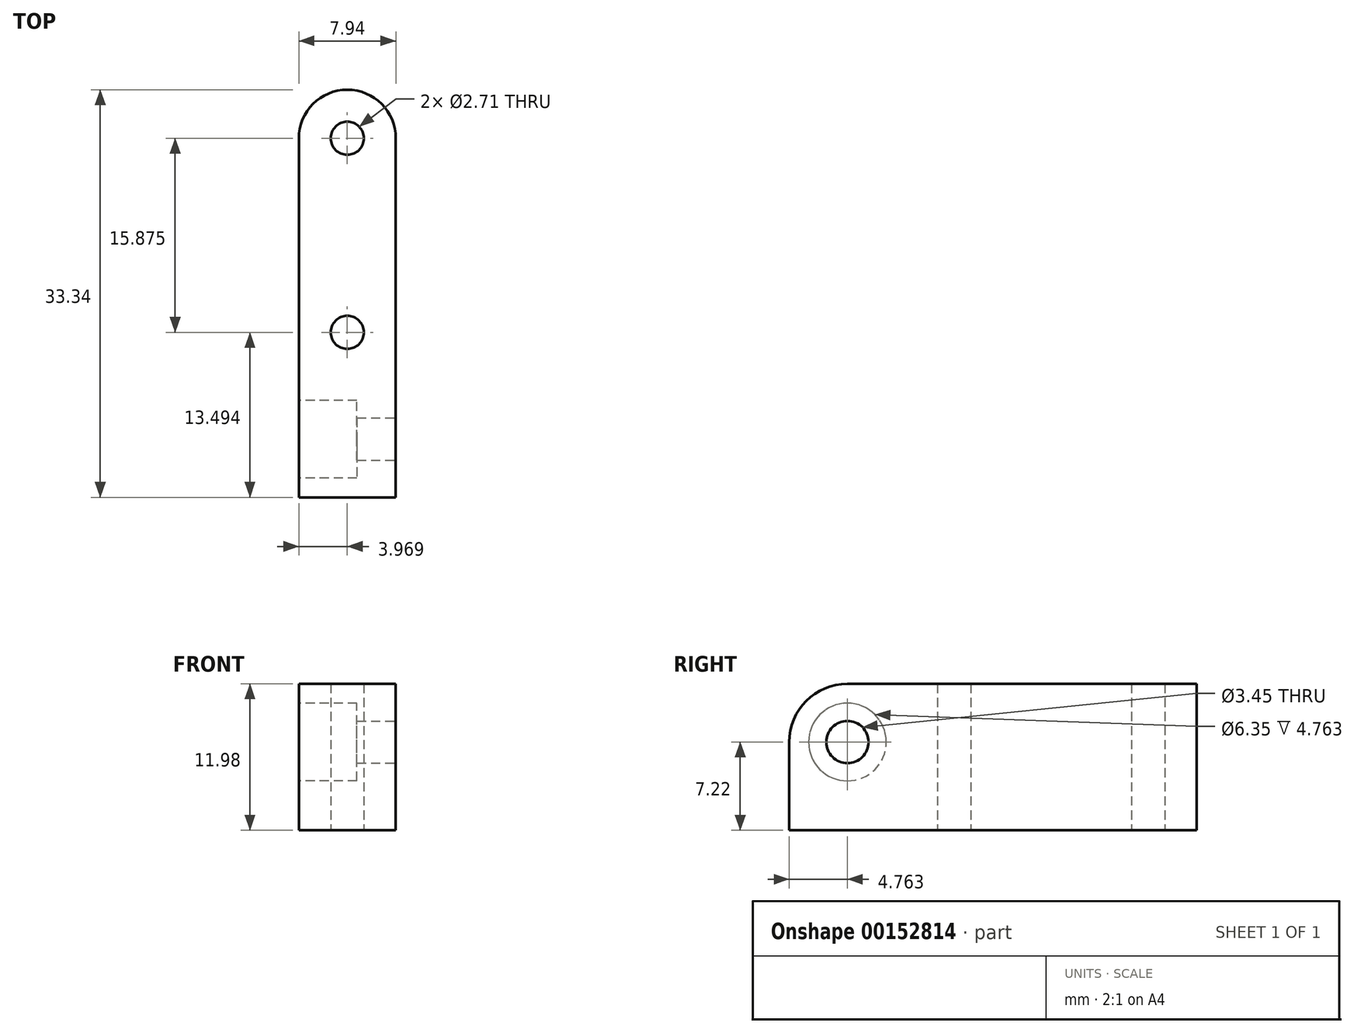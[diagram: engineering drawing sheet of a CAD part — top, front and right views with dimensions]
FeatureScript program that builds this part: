
annotation { "Feature Type Name" : "Feature", "Feature Type Description" : "" }
export const myFeature = defineFeature(function(context is Context, id is Id, definition is map)
    precondition{}
    {
        {
            var Q0;
            Q0=qCreatedBy(makeId("Top.planeOp"),FACE);
            var sketch = newSketch(context, id + "F0", { "sketchPlane" : qUnion([Q0])});
            skLineSegment(sketch, "E0.bottom", {"start": v(0, 0) * mm, "end": v(7.94, 0) * mm});
            skLineSegment(sketch, "E0.top", {"start": v(0, 33.34) * mm, "end": v(7.94, 33.34) * mm});
            skLineSegment(sketch, "E0.left", {"start": v(0, 0) * mm, "end": v(0, 33.34) * mm});
            skLineSegment(sketch, "E0.right", {"start": v(7.94, 0) * mm, "end": v(7.94, 33.34) * mm});
            skLineSegment(sketch, "E1", {"start": v(0, 29.37) * mm, "end": v(3.97, 29.37) * mm, "construction": true});
            skLineSegment(sketch, "E2", {"start": v(3.97, 29.37) * mm, "end": v(3.97, 33.34) * mm, "construction": true});
            skCircle(sketch, "E3", {"center": v(3.97, 29.37) * mm, "radius": 1.35 * mm});
            skLineSegment(sketch, "E4", {"start": v(3.97, 29.37) * mm, "end": v(3.97, 13.5) * mm, "construction": true});
            skCircle(sketch, "E5", {"center": v(3.97, 13.5) * mm, "radius": 1.35 * mm});
            skSolve(sketch);
        }
        {
            var Q0;
            Q0=qSketchRegion(id+"F0",true);
            extrude(context, id + "F1", {"entities" : qUnion([Q0]), "depth" : 11.98 * mm});
        }
        {
            var Q0;
            Q0=makeQuery(id+"F1.opExtrude","SWEPT_EDGE",EDGE,{"disambiguationData":[OSD([sQuery(id+"F0.wireOp",EDGE,"E0.top"),sQuery(id+"F0.wireOp",EDGE,"E0.right")])]});
            var Q1;
            Q1=makeQuery(id+"F1.opExtrude","SWEPT_EDGE",EDGE,{"disambiguationData":[OSD([sQuery(id+"F0.wireOp",EDGE,"E0.top"),sQuery(id+"F0.wireOp",EDGE,"E0.left")])]});
            fillet(context, id + "F2", {"entities" : qUnion([Q0, Q1]), "radius" : 3.97 * mm, "allowEdgeOverflow" : false});
        }
        {
            var Q0;
            Q0=makeQuery(id+"F1.opExtrude","CAP_EDGE",EDGE,{"disambiguationData":[OSD([sQuery(id+"F0.wireOp",EDGE,"E0.bottom")])],"isStart":false});
            fillet(context, id + "F3", {"entities" : qUnion([Q0]), "radius" : 4.76 * mm, "tangentPropagation" : true, "allowEdgeOverflow" : false});
        }
        {
            var Q0;
            Q0=makeQuery(id+"F1.opExtrude","SWEPT_FACE",FACE,{"disambiguationData":[OSD([sQuery(id+"F0.wireOp",EDGE,"E0.right")])]});
            var sketch = newSketch(context, id + "F4", { "sketchPlane" : qUnion([Q0])});
            skCircle(sketch, "E6", {"center": v(4.76, 7.22) * mm, "radius": 1.73 * mm});
            skSolve(sketch);
        }
        {
            var Q0;
            Q0 = qSketchRegion(id + "F4", true);
            var Q1;
            Q1=makeQuery(id+"F1.opExtrude","SWEPT_FACE",FACE,{"disambiguationData":[OSD([sQuery(id+"F0.wireOp",EDGE,"E0.left")])]});
            extrude(context, id + "F5", {"entities" : qUnion([Q0]), "operationType" : NewBodyOperationType.REMOVE, "endBound" : BoundingType.UP_TO_SURFACE, "oppositeDirection" : true, "endBoundEntityFace" : qUnion([Q1]), "depth" : 25.4 * mm});
        }
        {
            var Q0;
            Q0=makeQuery(id+"F1.opExtrude","SWEPT_FACE",FACE,{"disambiguationData":[OSD([sQuery(id+"F0.wireOp",EDGE,"E0.left")])]});
            var sketch = newSketch(context, id + "F6", { "sketchPlane" : qUnion([Q0])});
            skCircle(sketch, "E7", {"center": v(-4.76, 7.22) * mm, "radius": 3.18 * mm});
            skSolve(sketch);
        }
        {
            var Q0;
            Q0=makeQuery(id+"F1.opExtrude","SWEPT_FACE",FACE,{"disambiguationData":[OSD([sQuery(id+"F0.wireOp",EDGE,"E0.right")])]});
            cPlane(context, id + "F7", {"entities" : qUnion([Q0]), "cplaneType" : CPlaneType.OFFSET, "offset" : 3.17 * mm, "oppositeDirection" : true, "width" : 152.4 * mm, "height" : 152.4 * mm});
        }
        {
            var Q0;
            Q0=makeQuery(id+"F6.imprint","IMPRINT",FACE,{"disambiguationData":[TD([[makeQuery(id+"F6.imprint","IMPRINT",EDGE,{"derivedFrom":sQuery(id+"F6.wireOp",EDGE,"E7")}),1.0]])]});
            var Q1;
            Q1=qCreatedBy(id+"F7.planeOp",FACE);
            extrude(context, id + "F8", {"entities" : qUnion([Q0]), "operationType" : NewBodyOperationType.REMOVE, "endBound" : BoundingType.UP_TO_SURFACE, "oppositeDirection" : true, "endBoundEntityFace" : qUnion([Q1]), "depth" : 25.4 * mm});
        }
    });
